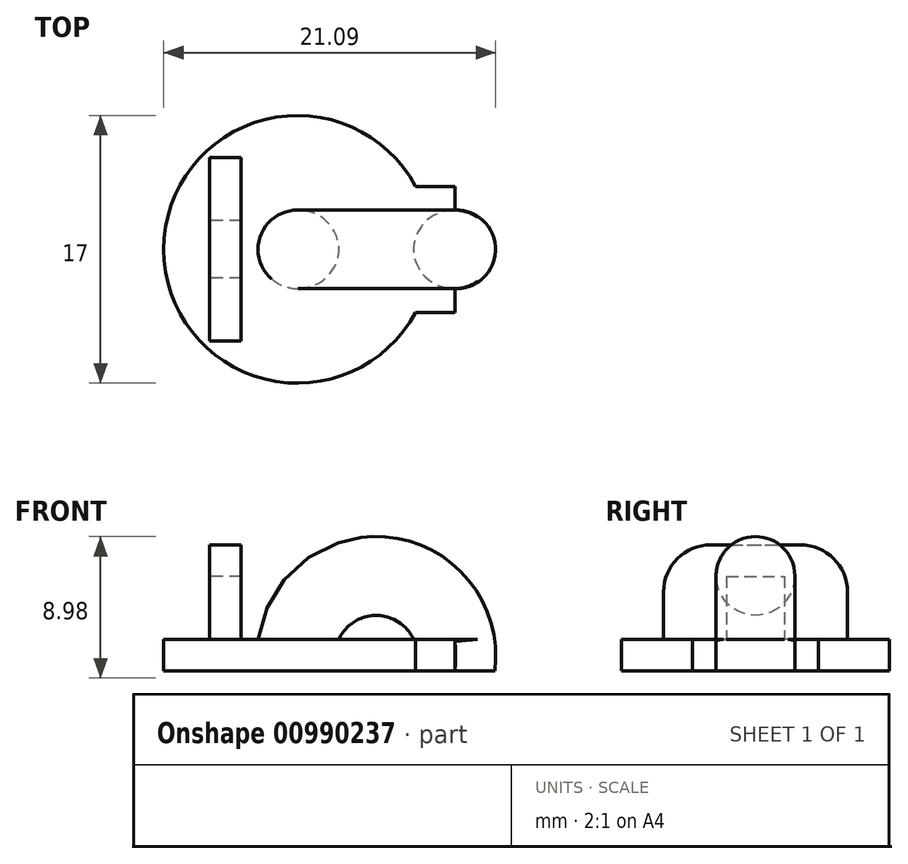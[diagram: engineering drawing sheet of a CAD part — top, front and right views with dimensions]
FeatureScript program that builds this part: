
annotation { "Feature Type Name" : "Feature", "Feature Type Description" : "" }
export const myFeature = defineFeature(function(context is Context, id is Id, definition is map)
    precondition{}
    {
        {
            var Q0;
            Q0=qCreatedBy(makeId("Top.planeOp"),FACE);
            var sketch = newSketch(context, id + "F0", { "sketchPlane" : qUnion([Q0])});
            skCircle(sketch, "E0", {"center": v(0, 0) * mm, "radius": 8.5 * mm});
            skLineSegment(sketch, "E1.bottom", {"start": v(0, 4) * mm, "end": v(10, 4) * mm});
            skLineSegment(sketch, "E1.top", {"start": v(0, -4) * mm, "end": v(10, -4) * mm});
            skLineSegment(sketch, "E1.left", {"start": v(0, 4) * mm, "end": v(0, -4) * mm});
            skLineSegment(sketch, "E1.right", {"start": v(10, 4) * mm, "end": v(10, -4) * mm});
            skCircle(sketch, "E2", {"center": v(10, 0) * mm, "radius": 2.5 * mm});
            skCircle(sketch, "E3", {"center": v(0, 0) * mm, "radius": 2.5 * mm});
            skLineSegment(sketch, "E4", {"start": v(10, 0) * mm, "end": v(0, 0) * mm, "construction": true});
            skLineSegment(sketch, "E5", {"start": v(5, 0) * mm, "end": v(5, 1.9) * mm, "construction": true});
            skSolve(sketch);
        }
        {
            var Q0;
            Q0=qSketchRegion(id+"F0",true);
            var Q1;
            {var subQ0=sQuery(id+"F0.wireOp",EDGE,"E2");var subQ1=sQuery(id+"F0.wireOp",EDGE,"E0");var subQ2=makeQuery(id+"F0.imprint","INTERSECT",VERTEX,{"disambiguationData":[OD(0.0)],"derivedFrom":[subQ1,subQ0]});Q1=makeQuery(id+"F0.imprint","IMPRINT",FACE,{"disambiguationData":[TD([[makeQuery(id+"F0.imprint","IMPRINT",EDGE,{"disambiguationData":[TD([[subQ2,1.0]])],"derivedFrom":subQ1}),1.0]])]});}
            var Q2;
            {var subQ0=sQuery(id+"F0.wireOp",EDGE,"E3");var subQ1=sQuery(id+"F0.wireOp",EDGE,"E1.left");var subQ2=makeQuery(id+"F0.imprint","INTERSECT",VERTEX,{"disambiguationData":[OD(0.0)],"derivedFrom":[subQ1,subQ0]});Q2=makeQuery(id+"F0.imprint","IMPRINT",FACE,{"disambiguationData":[TD([[makeQuery(id+"F0.imprint","IMPRINT",EDGE,{"disambiguationData":[TD([[subQ2,-1.0]])],"derivedFrom":subQ1}),1.0]])]});}
            var Q3;
            {var subQ0=sQuery(id+"F0.wireOp",EDGE,"E3");var subQ1=sQuery(id+"F0.wireOp",EDGE,"E1.left");var subQ2=makeQuery(id+"F0.imprint","INTERSECT",VERTEX,{"disambiguationData":[OD(0.0)],"derivedFrom":[subQ1,subQ0]});Q3=makeQuery(id+"F0.imprint","IMPRINT",FACE,{"disambiguationData":[TD([[makeQuery(id+"F0.imprint","IMPRINT",EDGE,{"disambiguationData":[TD([[subQ2,-1.0]])],"derivedFrom":subQ1}),-1.0]])]});}
            extrude(context, id + "F1", {"entities" : qUnion([Q0, Q1, Q2, Q3]), "depth" : 2 * mm, "offsetDistance" : 25 * mm});
        }
        {
            var Q0;
            Q0=sQuery(id+"F0.wireOp",EDGE,"E5");
            cPlane(context, id + "F2", {"entities" : qUnion([Q0]), "cplaneType" : CPlaneType.LINE_ANGLE, "offset" : 25 * mm, "angle" : 90 * degree, "width" : 150 * mm, "height" : 150 * mm});
        }
        {
            var Q0;
            Q0=qCreatedBy(id+"F2.planeOp",FACE);
            var sketch = newSketch(context, id + "F3", { "sketchPlane" : qUnion([Q0])});
            skLineSegment(sketch, "E6", {"start": v(0, 1.52) * mm, "end": v(0, 6.02) * mm});
            skCircle(sketch, "E7", {"center": v(0, 6.02) * mm, "radius": 2.5 * mm});
            skSolve(sketch);
        }
        {
            var Q0;
            Q0=sQuery(id+"F3.wireOp",EDGE,"E6");
            cPlane(context, id + "F4", {"entities" : qUnion([Q0]), "cplaneType" : CPlaneType.LINE_ANGLE, "offset" : 25 * mm, "angle" : 90 * degree, "width" : 150 * mm, "height" : 150 * mm});
        }
        {
            var Q0;
            Q0=qCreatedBy(id+"F4.planeOp",FACE);
            var sketch = newSketch(context, id + "F5", { "sketchPlane" : qUnion([Q0])});
            skPoint(sketch, "E8.0", {"position": v(0, 0) * mm});
            skPoint(sketch, "E9.0", {"position": v(-5, 6.02) * mm});
            skPoint(sketch, "E10.0", {"position": v(-10, 0) * mm});
            skArc(sketch, "E11", {"start": v(0, 0) * mm, "mid": v(-5, 6.02) * mm, "end": v(-10, 0) * mm});
            skSolve(sketch);
        }
        {
            var Q0;
            Q0=makeQuery(id+"F3.imprint","IMPRINT",FACE,{"disambiguationData":[TD([[makeQuery(id+"F3.imprint","IMPRINT",EDGE,{"derivedFrom":sQuery(id+"F3.wireOp",EDGE,"E7")}),1.0]])]});
            var Q1;
            Q1=sQuery(id+"F5.wireOp",EDGE,"E11");
            sweep(context, id + "F6", {"operationType" : NewBodyOperationType.ADD, "profiles" : qUnion([Q0]), "path" : qUnion([Q1])});
        }
        {
            var Q0;
            Q0=qCreatedBy(makeId("Top.planeOp"),FACE);
            var sketch = newSketch(context, id + "F7", { "sketchPlane" : qUnion([Q0])});
            skLineSegment(sketch, "E12.bottom", {"start": v(15.57, -10.06) * mm, "end": v(-15.57, -10.06) * mm});
            skLineSegment(sketch, "E12.top", {"start": v(15.57, 10.06) * mm, "end": v(-15.57, 10.06) * mm});
            skLineSegment(sketch, "E12.left", {"start": v(15.57, -10.06) * mm, "end": v(15.57, 10.06) * mm});
            skLineSegment(sketch, "E12.right", {"start": v(-15.57, -10.06) * mm, "end": v(-15.57, 10.06) * mm});
            skPoint(sketch, "E12.middle", {"position": v(0, 0) * mm});
            skSolve(sketch);
        }
        {
            var Q0;
            Q0=qSketchRegion(id+"F7",true);
            extrude(context, id + "F8", {"entities" : qUnion([Q0]), "operationType" : NewBodyOperationType.REMOVE, "oppositeDirection" : true, "depth" : 25 * mm, "offsetDistance" : 25 * mm});
        }
        {
            var Q0;
            Q0=makeQuery(id+"F1.opExtrude","CAP_FACE",FACE,{"disambiguationData":[OSD([sQuery(id+"F0.wireOp",EDGE,"E0"),sQuery(id+"F0.wireOp",EDGE,"E1.bottom"),sQuery(id+"F0.wireOp",EDGE,"E1.top"),sQuery(id+"F0.wireOp",EDGE,"E1.right"),sQuery(id+"F0.wireOp",EDGE,"E2")])],"isStart":false});
            var sketch = newSketch(context, id + "F9", { "sketchPlane" : qUnion([Q0])});
            skLineSegment(sketch, "E13", {"start": v(0, 0) * mm, "end": v(-4.57, 3.84) * mm});
            skLineSegment(sketch, "E14", {"start": v(0, 0) * mm, "end": v(-5, 0) * mm, "construction": true});
            skLineSegment(sketch, "E15.MirrorCS", {"start": v(0, 0) * mm, "end": v(-4.57, -3.84) * mm});
            skLineSegment(sketch, "E16.bottom", {"start": v(-3.57, 1.84) * mm, "end": v(-5.57, 1.84) * mm});
            skLineSegment(sketch, "E16.top", {"start": v(-3.57, 5.84) * mm, "end": v(-5.57, 5.84) * mm});
            skLineSegment(sketch, "E16.left", {"start": v(-3.57, 1.84) * mm, "end": v(-3.57, 5.84) * mm});
            skLineSegment(sketch, "E16.right", {"start": v(-5.57, 1.84) * mm, "end": v(-5.57, 5.84) * mm});
            skPoint(sketch, "E16.middle", {"position": v(-4.57, 3.84) * mm});
            skLineSegment(sketch, "E17.MirrorCS", {"start": v(-3.57, -1.84) * mm, "end": v(-5.57, -1.84) * mm});
            skLineSegment(sketch, "E18.MirrorCS", {"start": v(-3.57, -1.84) * mm, "end": v(-3.57, -5.84) * mm});
            skLineSegment(sketch, "E19.MirrorCS", {"start": v(-3.57, -5.84) * mm, "end": v(-5.57, -5.84) * mm});
            skLineSegment(sketch, "E20.MirrorCS", {"start": v(-5.57, -1.84) * mm, "end": v(-5.57, -5.84) * mm});
            skSolve(sketch);
        }
        {
            var Q0;
            {var subQ3=sQuery(id+"F9.wireOp",EDGE,"E16.bottom");Q0=makeQuery(id+"F9.imprint","IMPRINT",FACE,{"disambiguationData":[TD([[makeQuery(id+"F9.imprint","IMPRINT",EDGE,{"derivedFrom":subQ3}),-1.0]])]});}
            var Q1;
            {var subQ3=sQuery(id+"F9.wireOp",EDGE,"E17.MirrorCS");Q1=makeQuery(id+"F9.imprint","IMPRINT",FACE,{"disambiguationData":[TD([[makeQuery(id+"F9.imprint","IMPRINT",EDGE,{"derivedFrom":subQ3}),1.0]])]});}
            extrude(context, id + "F10", {"entities" : qUnion([Q0, Q1]), "operationType" : NewBodyOperationType.ADD, "depth" : 4 * mm, "offsetDistance" : 25 * mm});
        }
        {
            var Q0;
            Q0=makeQuery(id+"F10.opExtrude","CAP_FACE",FACE,{"disambiguationData":[OSD([sQuery(id+"F9.wireOp",EDGE,"E16.bottom"),sQuery(id+"F9.wireOp",EDGE,"E16.top"),sQuery(id+"F9.wireOp",EDGE,"E16.left"),sQuery(id+"F9.wireOp",EDGE,"E16.right")])],"isStart":false});
            var sketch = newSketch(context, id + "F11", { "sketchPlane" : qUnion([Q0])});
            skPoint(sketch, "E21.0", {"position": v(-5.57, 5.84) * mm});
            skPoint(sketch, "E22.0", {"position": v(-3.57, -5.84) * mm});
            skLineSegment(sketch, "E23.bottom", {"start": v(-5.57, 5.84) * mm, "end": v(-3.57, 5.84) * mm});
            skLineSegment(sketch, "E23.top", {"start": v(-5.57, -5.84) * mm, "end": v(-3.57, -5.84) * mm});
            skLineSegment(sketch, "E23.left", {"start": v(-5.57, 5.84) * mm, "end": v(-5.57, -5.84) * mm});
            skLineSegment(sketch, "E23.right", {"start": v(-3.57, 5.84) * mm, "end": v(-3.57, -5.84) * mm});
            skSolve(sketch);
        }
        {
            var Q0;
            Q0=qSketchRegion(id+"F11",true);
            extrude(context, id + "F12", {"entities" : qUnion([Q0]), "operationType" : NewBodyOperationType.ADD, "depth" : 2 * mm, "offsetDistance" : 25 * mm});
        }
        {
            var Q0;
            Q0=makeQuery(id+"F12.opExtrude","CAP_EDGE",EDGE,{"disambiguationData":[OSD([sQuery(id+"F11.wireOp",EDGE,"E23.top")])],"isStart":false});
            var Q1;
            Q1=makeQuery(id+"F12.opExtrude","CAP_EDGE",EDGE,{"disambiguationData":[OSD([sQuery(id+"F11.wireOp",EDGE,"E23.bottom")])],"isStart":false});
            fillet(context, id + "F13", {"entities" : qUnion([Q0, Q1]), "radius" : 3 * mm, "tangentPropagation" : true, "allowEdgeOverflow" : false});
        }
    });
